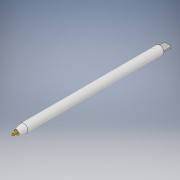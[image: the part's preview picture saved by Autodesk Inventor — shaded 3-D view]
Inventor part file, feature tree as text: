
AUTODESK INVENTOR PART (.ipt)
format: ipt  version: 2018 (Build 220112000, 112)  size: 158,208 bytes
history: native  units: in
note: dims shown in document units (in); Inventor stores cm internally (conversion verified against a paired STEP export)
features: sketch x3, revolve x1, extrude x1, fillet x1, chamfer x1
ambient origin geometry x8: Origin, YZ Plane, XZ Plane, XY Plane, X Axis, Y Axis, Z Axis, Center Point
bodies: Solid1 (feature_tree)
feature tree (7):
  revolve  "Revolution1"  [1 undecoded]
  extrude  "Extrusion1"  Depth=0.05in
  fillet  "Fillet1"  Radius=0.055in
  chamfer  "Chamfer1"  Distance=0.3in
  sketch  "Sketch3"  dims[d5=0.1in d6=0.3in d7=0.175in d8=0.175in d9=0.01in d10=0.15in d11=0.24in d12=90.0deg d13=0.03in d14=0.03in d15=0.35in d16=0.0in d17=0.04in d18=0.04in d19=0.02in d20=45.0deg d21=0.0097in]
  sketch  "Sketch1"  dims[d0=6.0in d1=0.2in]
  sketch  "Sketch2"  dims[d2=0.05in d3=0.19in d4=0.055in]
note: 1 required parameter value undecoded (feature->parameter linkage not recoverable at this tier; creation-order binding heuristic only, values carry confidence <= 0.55)
